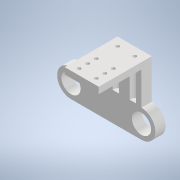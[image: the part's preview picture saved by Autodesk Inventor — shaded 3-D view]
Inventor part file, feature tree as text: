
AUTODESK INVENTOR PART (.ipt)
format: ipt  version: 2020 (Build 240168000, 168)  size: 226,816 bytes
history: native  units: in
note: dims shown in document units (in); Inventor stores cm internally (conversion verified against a paired STEP export)
features: extrude x6, sketch x5, plane x1
ambient origin geometry x8: Origin, YZ Plane, XZ Plane, XY Plane, X Axis, Y Axis, Z Axis, Center Point
bodies: Solid1 (feature_tree)
feature tree (12):
  extrude  "Extrusion1"  Depth=0.813in
  extrude  "Extrusion2"  Depth=0.6in
  extrude  "Extrusion3"  Depth=2.0in
  extrude  "Extrusion4"  Depth=4.125in
  extrude  "Extrusion5"  Depth=1.0in TaperAngle=0.0deg
  plane  "Work Plane1"
  extrude  "Extrusion6"  Depth=0.375in
  sketch  "Sketch1"  dims[d0=4.125in d1=0.813in]
  sketch  "Sketch2"  dims[d2=0.6in d3=0.0in d4=1.126in]
  sketch  "Sketch3"  dims[d5=0.0in d6=0.0in d7=2.0in]
  sketch  "Sketch4"  dims[d8=0.875in d9=4.125in]
  sketch  "Sketch6"  dims[d10=3.127in d11=1.0in d12=0.0in d13=0.375in d14=2.5in d15=0.0in d17=0.2031in d18=0.5in d19=0.7874in d21=1.0in d22=0.7874in d24=1.25in d27=1.1811in d29=0.5in d30=0.3937in d32=1.0in d34=2.0in d35=0.0in d36=-0.25in d47=0.25in d48=0.1875in d49=2.0in d50=0.0in d51=0.5in]
